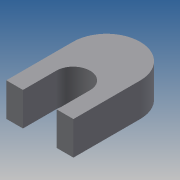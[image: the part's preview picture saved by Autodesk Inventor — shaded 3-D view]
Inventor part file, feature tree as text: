
AUTODESK INVENTOR PART (.ipt)
format: ipt  version: 2014 (Build 180170000, 170)  size: 79,360 bytes
history: native  units: mm
features: extrude x1, sketch x1
ambient origin geometry x8: Origin, YZ Plane, XZ Plane, XY Plane, X Axis, Y Axis, Z Axis, Center Point
bodies: Solid1 (feature_tree)
feature tree (2):
  extrude  "Extrusion1"  Depth=4.0mm
  sketch  "Sketch1"  dims[d0=4.05mm d1=8.0mm d3=2.0mm d4=4.0mm d5=4.0mm d6=0.0mm]
